# Revit family: 1437xxx - Keta UL
name_source: partatom
category: Lighting Fixtures
units: mm (PartAtom-declared; Revit-internal decimal feet)

## family parameters
Always vertical = Yes
Cut with Voids When Loaded = No
Host = Wall
Light Source = Yes
OmniClass Number = 23.80.70.00
OmniClass Title = Lighting
Part Type = Normal
Room Calculation Point = No
Round Connector Dimension = Use Diameter
Shared = No

## types (2) — shared parameters
Color Filter = 16777215
Dimmable = No
Dimming Lamp Color Temperature Shift = <None>
Dimming Method = Not Applicable
Driver Included = Integrated
Driver Required = No
Efficacy (lm/w) = 53
Electrical Class = 1
Lamp = LED
Length of Cable Supplied = Not Applicable
Light Source Fixed = Adjustable
Main Finish = Matt Nickel
Main Material = Metal - Zinc
Manufacturer = Astro Lighting Ltd
Manufacturer URL - Europe and Rest of World = www.astrolighting.com
Manufacturer URL - North America = us.astrolighting.com
Power (Watts) = 3.2
Product CCT = 2700K
Product CRI = 90
Product Dimensions (MM) = 256 x 63 x 67
Product Location = Wall
Product Name = Keta
Tilt Angle = 60.00°
URL = www.astrolighting.com
zero-valued in all types: Default Elevation

## per-type parameters (varying)
| type | ADA compliant | Location / IP Rating | Photometric Web File | Product SKU | Product Weight (KG) |
| CE | N / A | Indoor / IP20 | 1437001_Keta Matt Nickel__Photometry_IES_Iss.01.ies | 1437001 | 0.724 |
| ETL | Yes | Indoor / Dry | 1437002_Keta Matt Nickel__Photometry_IES_Iss.01.ies | 1437002 | 0.962 |

## geometry (parser evidence)
native form markers: Sweep x3
no freeform markers — native parametric forms only
